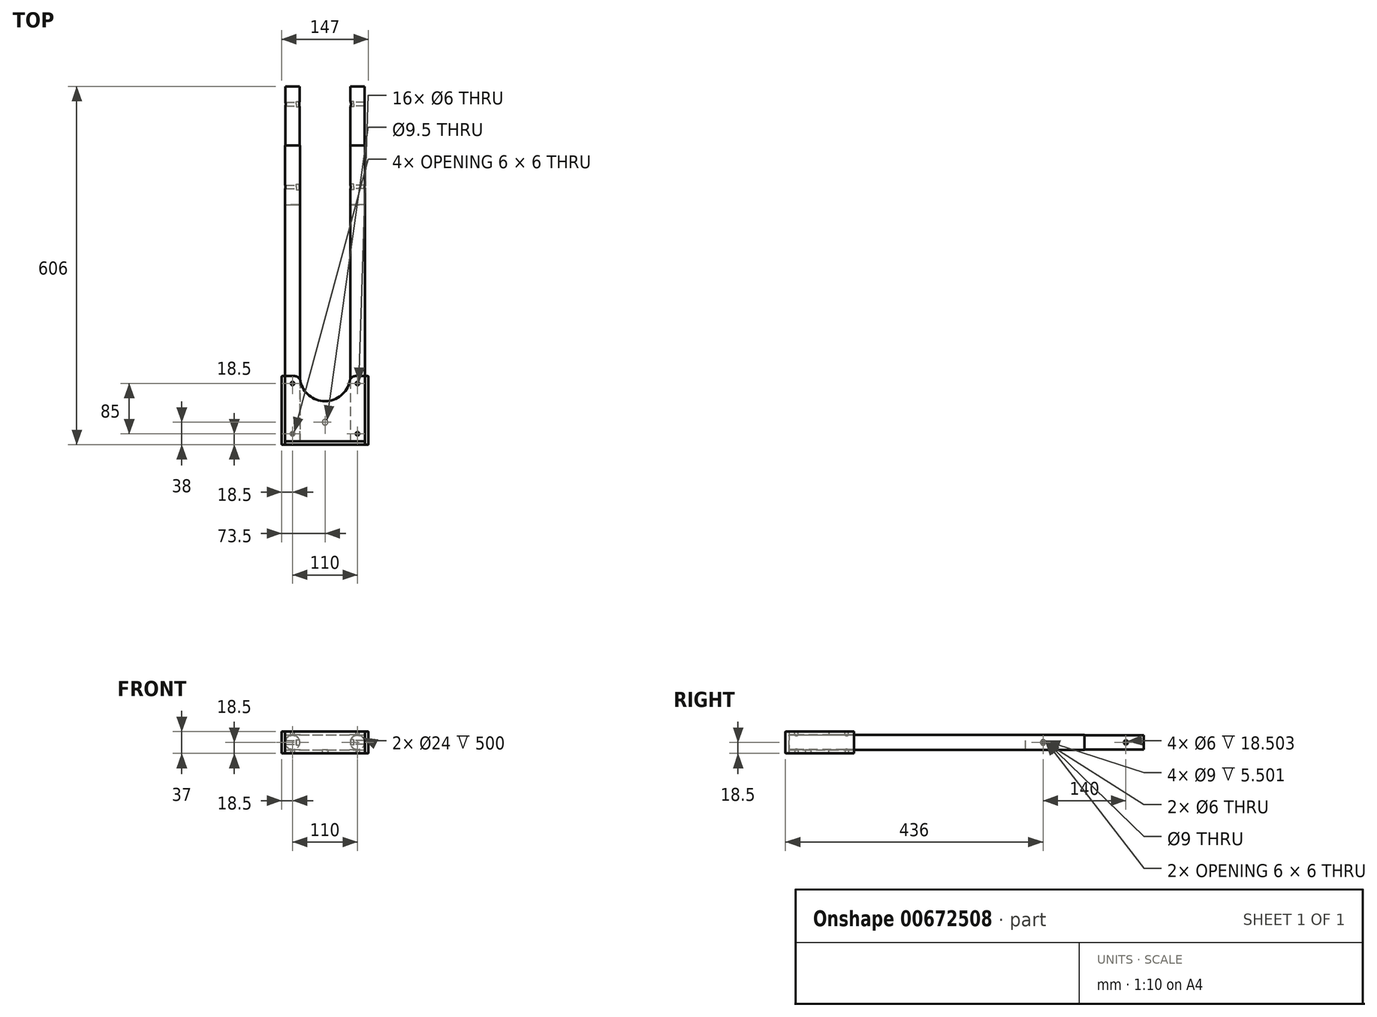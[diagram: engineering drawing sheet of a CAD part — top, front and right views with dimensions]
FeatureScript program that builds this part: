
annotation { "Feature Type Name" : "Feature", "Feature Type Description" : "" }
export const myFeature = defineFeature(function(context is Context, id is Id, definition is map)
    precondition{}
    {
        {
            var Q0;
            Q0=qCreatedBy(makeId("Front.planeOp"),FACE);
            var sketch = newSketch(context, id + "F0", { "sketchPlane" : qUnion([Q0])});
            skLineSegment(sketch, "E0", {"start": v(0, 0) * mm, "end": v(-55, 0) * mm, "construction": true});
            skCircle(sketch, "E1", {"center": v(-55, 0) * mm, "radius": 12.5 * mm});
            skCircle(sketch, "E2", {"center": v(-55, 0) * mm, "radius": 12 * mm});
            skSolve(sketch);
        }
        {
            var Q0;
            Q0=qSketchRegion(id+"F0",true);
            extrude(context, id + "F1", {"entities" : qUnion([Q0]), "oppositeDirection" : true, "depth" : 500 * mm, "offsetDistance" : 25 * mm});
        }
        {
            var Q0;
            Q0=qCreatedBy(makeId("Right.planeOp"),FACE);
            cPlane(context, id + "F2", {"entities" : qUnion([Q0]), "cplaneType" : CPlaneType.OFFSET, "offset" : 67.5 * mm, "oppositeDirection" : true, "width" : 150 * mm, "height" : 150 * mm});
        }
        {
            var Q0;
            Q0=qCreatedBy(id+"F2.planeOp",FACE);
            var sketch = newSketch(context, id + "F3", { "sketchPlane" : qUnion([Q0])});
            skCircle(sketch, "E3", {"center": v(430, 0) * mm, "radius": 3 * mm});
            skSolve(sketch);
        }
        {
            var Q0;
            Q0 = qSketchRegion(id + "F3", true);
            extrude(context, id + "F4", {"entities" : qUnion([Q0]), "operationType" : NewBodyOperationType.REMOVE, "depth" : 5 * mm, "offsetDistance" : 25 * mm});
        }
        {
            var Q0;
            Q0=makeQuery(id+"F1.opExtrude","SWEPT_BODY",BODY,{"disambiguationData":[OSD([sQuery(id+"F0.wireOp",EDGE,"E1"),sQuery(id+"F0.wireOp",EDGE,"E2")])]});
            var Q1;
            Q1=makeQuery(id+"FWwEWK0AGCShoOY_4.opExtrude","SWEPT_BODY",BODY,{"disambiguationData":[OSD([sQuery(id+"Fcy4laaUm5Z0fuw_4.wireOp",EDGE,"4f178126-5fd6-475b-9708-48581a11361a.0")])]});
            var Q2;
            Q2=qCreatedBy(makeId("Right.planeOp"),FACE);
            mirror(context, id + "F5", {"entities" : qUnion([Q0, Q1]), "mirrorPlane" : qUnion([Q2])});
        }
        {
            var Q0;
            Q0=qCreatedBy(makeId("Top.planeOp"),FACE);
            cPlane(context, id + "F6", {"entities" : qUnion([Q0]), "cplaneType" : CPlaneType.OFFSET, "offset" : 12.5 * mm, "oppositeDirection" : true, "width" : 150 * mm, "height" : 150 * mm});
        }
        {
            var Q0;
            Q0=qCreatedBy(id+"F6.planeOp",FACE);
            var sketch = newSketch(context, id + "F7", { "sketchPlane" : qUnion([Q0])});
            skLineSegment(sketch, "E4", {"start": v(-67.5, 0) * mm, "end": v(-67.5, 500) * mm, "construction": true});
            skLineSegment(sketch, "E5", {"start": v(67.5, 500) * mm, "end": v(67.5, 0) * mm, "construction": true});
            skLineSegment(sketch, "E6.top", {"start": v(-67.5, 110) * mm, "end": v(-42.5, 110) * mm});
            skLineSegment(sketch, "E6.left", {"start": v(-67.5, 0) * mm, "end": v(-67.5, 110) * mm});
            skLineSegment(sketch, "E6.right", {"start": v(67.5, 0) * mm, "end": v(67.5, 110) * mm});
            skArc(sketch, "E7", {"start": v(-42.5, 110) * mm, "mid": v(0, 67.5) * mm, "end": v(42.5, 110) * mm});
            skLineSegment(sketch, "E8.trimOffspring", {"start": v(42.5, 110) * mm, "end": v(67.5, 110) * mm});
            skLineSegment(sketch, "E9", {"start": v(-67.5, 0) * mm, "end": v(67.5, 0) * mm});
            skSolve(sketch);
        }
        {
            var Q0;
            Q0 = qSketchRegion(id + "F7", true);
            extrude(context, id + "F8", {"entities" : qUnion([Q0]), "oppositeDirection" : true, "depth" : 6 * mm, "offsetDistance" : 25 * mm});
        }
        {
            var Q0;
            Q0=makeQuery(id+"F8.opExtrude","SWEPT_EDGE",EDGE,{"disambiguationData":[OSD([sQuery(id+"F7.wireOp",EDGE,"E6.top"),sQuery(id+"F7.wireOp",EDGE,"E7")])]});
            var Q1;
            Q1=makeQuery(id+"F8.opExtrude","SWEPT_EDGE",EDGE,{"disambiguationData":[OSD([sQuery(id+"F7.wireOp",EDGE,"E7"),sQuery(id+"F7.wireOp",EDGE,"E8.trimOffspring")])]});
            fillet(context, id + "F9", {"entities" : qUnion([Q0, Q1]), "radius" : 10 * mm, "tangentPropagation" : true, "allowEdgeOverflow" : false});
        }
        {
            var Q0;
            Q0=makeQuery(id+"F8.opExtrude","CAP_FACE",FACE,{"disambiguationData":[OSD([sQuery(id+"F7.wireOp",EDGE,"E6.top"),sQuery(id+"F7.wireOp",EDGE,"E6.left"),sQuery(id+"F7.wireOp",EDGE,"E6.right"),sQuery(id+"F7.wireOp",EDGE,"E7"),sQuery(id+"F7.wireOp",EDGE,"E8.trimOffspring"),sQuery(id+"F7.wireOp",EDGE,"0f04a0eb-fee5-4bae-b65f-fa6f64b50764.0"),sQuery(id+"F7.wireOp",EDGE,"cbebf984-d675-44ab-9455-374cf201430f.0"),sQuery(id+"F7.wireOp",EDGE,"HSed2Bmm-BiSO-eANn-IlEf-6T3VpWwfTWnc")])],"isStart":false});
            var sketch = newSketch(context, id + "F10", { "sketchPlane" : qUnion([Q0])});
            skCircle(sketch, "E10", {"center": v(-55, -12.5) * mm, "radius": 3 * mm});
            skCircle(sketch, "E11", {"center": v(-55, -97.5) * mm, "radius": 3 * mm});
            skCircle(sketch, "E12", {"center": v(55, -97.5) * mm, "radius": 3 * mm});
            skCircle(sketch, "E13", {"center": v(55, -12.5) * mm, "radius": 3 * mm});
            skSolve(sketch);
        }
        {
            var Q0;
            Q0 = qSketchRegion(id + "F10", true);
            extrude(context, id + "F11", {"entities" : qUnion([Q0]), "operationType" : NewBodyOperationType.REMOVE, "endBound" : BoundingType.THROUGH_ALL, "oppositeDirection" : true, "depth" : 10 * mm, "offsetDistance" : 25 * mm});
        }
        {
            var Q0;
            Q0=makeQuery(id+"F8.opExtrude","SWEPT_BODY",BODY,{"disambiguationData":[OSD([sQuery(id+"F7.wireOp",EDGE,"E6.bottom"),sQuery(id+"F7.wireOp",EDGE,"E6.top"),sQuery(id+"F7.wireOp",EDGE,"E6.left"),sQuery(id+"F7.wireOp",EDGE,"E6.right"),sQuery(id+"F7.wireOp",EDGE,"E7"),sQuery(id+"F7.wireOp",EDGE,"E8.trimOffspring")])]});
            var Q1;
            Q1=qCreatedBy(makeId("Top.planeOp"),FACE);
            mirror(context, id + "F12", {"entities" : qUnion([Q0]), "mirrorPlane" : qUnion([Q1])});
        }
        {
            var Q0;
            Q0=makeQuery(id+"F5.opPattern","COPY",FACE,{"derivedFrom":makeQuery(id+"F1.opExtrude","CAP_FACE",FACE,{"disambiguationData":[OSD([sQuery(id+"F0.wireOp",EDGE,"E1"),sQuery(id+"F0.wireOp",EDGE,"E2")])],"isStart":false}),"instanceName":"1"});
            var sketch = newSketch(context, id + "F13", { "sketchPlane" : qUnion([Q0])});
            skCircle(sketch, "E14.0", {"center": v(-55, 0) * mm, "radius": 12 * mm});
            skSolve(sketch);
        }
        {
            var Q0;
            Q0 = qSketchRegion(id + "F13", true);
            extrude(context, id + "F14", {"entities" : qUnion([Q0]), "endBound" : BoundingType.SYMMETRIC, "depth" : 200 * mm, "offsetDistance" : 25 * mm});
        }
        {
            var Q0;
            Q0=qCreatedBy(makeId("Right.planeOp"),FACE);
            cPlane(context, id + "F15", {"entities" : qUnion([Q0]), "cplaneType" : CPlaneType.OFFSET, "offset" : 42.5 * mm, "width" : 150 * mm, "height" : 150 * mm});
        }
        {
            var Q0;
            Q0=qCreatedBy(id+"F15.planeOp",FACE);
            var sketch = newSketch(context, id + "F16", { "sketchPlane" : qUnion([Q0])});
            skLineSegment(sketch, "E15.0", {"start": v(400, 12) * mm, "end": v(400, -12) * mm, "construction": true});
            skCircle(sketch, "E16", {"center": v(430, 0) * mm, "radius": 3 * mm});
            skLineSegment(sketch, "E17.0", {"start": v(600, 12) * mm, "end": v(600, -12) * mm, "construction": true});
            skCircle(sketch, "E18", {"center": v(570, 0) * mm, "radius": 3 * mm});
            skSolve(sketch);
        }
        {
            var Q0;
            Q0 = qSketchRegion(id + "F16", true);
            extrude(context, id + "F17", {"entities" : qUnion([Q0]), "operationType" : NewBodyOperationType.REMOVE, "endBound" : BoundingType.THROUGH_ALL, "depth" : 25 * mm, "offsetDistance" : 25 * mm});
        }
        {
            var Q0;
            Q0=qCreatedBy(id+"F15.planeOp",FACE);
            var sketch = newSketch(context, id + "F18", { "sketchPlane" : qUnion([Q0])});
            skLineSegment(sketch, "E19", {"start": v(400, 12) * mm, "end": v(600, 12) * mm, "construction": true});
            skLineSegment(sketch, "E20", {"start": v(600, -12) * mm, "end": v(400, -12) * mm, "construction": true});
            skCircle(sketch, "E21.0", {"center": v(430, 0) * mm, "radius": 3 * mm, "construction": true});
            skCircle(sketch, "E22", {"center": v(430, 0) * mm, "radius": 4.5 * mm});
            skCircle(sketch, "E23.0", {"center": v(570, 0) * mm, "radius": 3 * mm, "construction": true});
            skCircle(sketch, "E24", {"center": v(570, 0) * mm, "radius": 4.5 * mm});
            skSolve(sketch);
        }
        {
            var Q0;
            Q0 = qSketchRegion(id + "F18", true);
            extrude(context, id + "F19", {"entities" : qUnion([Q0]), "operationType" : NewBodyOperationType.REMOVE, "depth" : 6 * mm, "offsetDistance" : 25 * mm});
        }
        {
            var Q0;
            Q0=makeQuery(id+"F14.opExtrude","SWEPT_BODY",BODY,{"disambiguationData":[OSD([sQuery(id+"F13.wireOp",EDGE,"E14.0")])]});
            var Q1;
            Q1=qCreatedBy(makeId("Right.planeOp"),FACE);
            mirror(context, id + "F20", {"entities" : qUnion([Q0]), "mirrorPlane" : qUnion([Q1])});
        }
        {
            var Q0;
            Q0=makeQuery(id+"F8.opExtrude","CAP_FACE",FACE,{"disambiguationData":[OSD([sQuery(id+"F7.wireOp",EDGE,"E6.top"),sQuery(id+"F7.wireOp",EDGE,"E6.left"),sQuery(id+"F7.wireOp",EDGE,"E6.right"),sQuery(id+"F7.wireOp",EDGE,"E7"),sQuery(id+"F7.wireOp",EDGE,"E8.trimOffspring"),sQuery(id+"F7.wireOp",EDGE,"d265e3d1-651c-44ed-b3ba-1d22781fd949.0"),sQuery(id+"F7.wireOp",EDGE,"8f73bf23-1377-4b1a-b3f5-81651f57eb4c.0"),sQuery(id+"F7.wireOp",EDGE,"ulxtdSOa-0rmS-N41F-JQdx-JKkltLVyDlMm"),sQuery(id+"F7.wireOp",EDGE,"lsUfgYp3-Q0MO-jZHI-4MhV-vEVjAvu659Rx"),sQuery(id+"F7.wireOp",EDGE,"MI6NjhT9-Nfcn-xXMY-YQLx-c0En6gxI8AMg")])],"isStart":false});
            var sketch = newSketch(context, id + "F21", { "sketchPlane" : qUnion([Q0])});
            skCircle(sketch, "E25", {"center": v(0, -32) * mm, "radius": 4.75 * mm});
            skSolve(sketch);
        }
        {
            var Q0;
            Q0 = qSketchRegion(id + "F21", true);
            extrude(context, id + "F22", {"entities" : qUnion([Q0]), "operationType" : NewBodyOperationType.REMOVE, "endBound" : BoundingType.UP_TO_NEXT, "oppositeDirection" : true, "depth" : 25 * mm, "offsetDistance" : 25 * mm});
        }
        {
            var Q0;
            Q0=makeQuery(id+"F12.opPattern","COPY",FACE,{"derivedFrom":makeQuery(id+"F8.opExtrude","SWEPT_FACE",FACE,{"disambiguationData":[OSD([sQuery(id+"F7.wireOp",EDGE,"E9")])]}),"instanceName":"1"});
            var sketch = newSketch(context, id + "F23", { "sketchPlane" : qUnion([Q0])});
            skPoint(sketch, "E26.0", {"position": v(67.5, -18.5) * mm});
            skLineSegment(sketch, "E27.bottom", {"start": v(-67.5, 18.5) * mm, "end": v(67.5, 18.5) * mm});
            skLineSegment(sketch, "E27.top", {"start": v(-67.5, -18.5) * mm, "end": v(67.5, -18.5) * mm});
            skLineSegment(sketch, "E27.left", {"start": v(-67.5, 18.5) * mm, "end": v(-67.5, -18.5) * mm});
            skLineSegment(sketch, "E27.right", {"start": v(67.5, 18.5) * mm, "end": v(67.5, -18.5) * mm});
            skSolve(sketch);
        }
        {
            var Q0;
            Q0 = qSketchRegion(id + "F23", true);
            extrude(context, id + "F24", {"entities" : qUnion([Q0]), "depth" : 6 * mm, "offsetDistance" : 25 * mm});
        }
        {
            var Q0;
            Q0=makeQuery(id+"F12.opPattern","COPY",FACE,{"derivedFrom":makeQuery(id+"F8.opExtrude","SWEPT_FACE",FACE,{"disambiguationData":[OSD([sQuery(id+"F7.wireOp",EDGE,"E6.left")])]}),"instanceName":"1"});
            var sketch = newSketch(context, id + "F25", { "sketchPlane" : qUnion([Q0])});
            skPoint(sketch, "E28.0", {"position": v(6, -18.5) * mm});
            skLineSegment(sketch, "E29.bottom", {"start": v(-110, 18.5) * mm, "end": v(6, 18.5) * mm});
            skLineSegment(sketch, "E29.top", {"start": v(-110, -18.5) * mm, "end": v(6, -18.5) * mm});
            skLineSegment(sketch, "E29.left", {"start": v(-110, 18.5) * mm, "end": v(-110, -18.5) * mm});
            skLineSegment(sketch, "E29.right", {"start": v(6, 18.5) * mm, "end": v(6, -18.5) * mm});
            skSolve(sketch);
        }
        {
            var Q0;
            Q0 = qSketchRegion(id + "F25", true);
            extrude(context, id + "F26", {"entities" : qUnion([Q0]), "depth" : 6 * mm, "offsetDistance" : 25 * mm});
        }
        {
            var Q0;
            Q0=makeQuery(id+"F26.opExtrude","SWEPT_BODY",BODY,{"disambiguationData":[OSD([sQuery(id+"F25.wireOp",EDGE,"E29.bottom"),sQuery(id+"F25.wireOp",EDGE,"E29.top"),sQuery(id+"F25.wireOp",EDGE,"E29.left"),sQuery(id+"F25.wireOp",EDGE,"E29.right")])]});
            var Q1;
            Q1=qCreatedBy(makeId("Right.planeOp"),FACE);
            mirror(context, id + "F27", {"entities" : qUnion([Q0]), "mirrorPlane" : qUnion([Q1])});
        }
        {
            var Q0;
            Q0=makeQuery(id+"F24.opExtrude","CAP_EDGE",EDGE,{"disambiguationData":[OSD([sQuery(id+"F23.wireOp",EDGE,"E27.bottom")])],"isStart":false});
            var Q1;
            Q1=makeQuery(id+"F27.opPattern","COPY",EDGE,{"derivedFrom":makeQuery(id+"F26.opExtrude","CAP_EDGE",EDGE,{"disambiguationData":[OSD([sQuery(id+"F25.wireOp",EDGE,"E29.bottom")])],"isStart":false}),"instanceName":"1"});
            var Q2;
            Q2=makeQuery(id+"F27.opPattern","COPY",EDGE,{"derivedFrom":makeQuery(id+"F26.opExtrude","SWEPT_EDGE",EDGE,{"disambiguationData":[OSD([sQuery(id+"F25.wireOp",EDGE,"E29.bottom"),sQuery(id+"F25.wireOp",EDGE,"E29.right")])]}),"instanceName":"1"});
            var Q3;
            Q3=makeQuery(id+"F27.opPattern","COPY",EDGE,{"derivedFrom":makeQuery(id+"F26.opExtrude","CAP_EDGE",EDGE,{"disambiguationData":[OSD([sQuery(id+"F25.wireOp",EDGE,"E29.right")])],"isStart":false}),"instanceName":"1"});
            var Q4;
            Q4=makeQuery(id+"F27.opPattern","COPY",EDGE,{"derivedFrom":makeQuery(id+"F26.opExtrude","CAP_EDGE",EDGE,{"disambiguationData":[OSD([sQuery(id+"F25.wireOp",EDGE,"E29.left")])],"isStart":false}),"instanceName":"1"});
            var Q5;
            Q5=makeQuery(id+"F27.opPattern","COPY",EDGE,{"derivedFrom":makeQuery(id+"F26.opExtrude","CAP_EDGE",EDGE,{"disambiguationData":[OSD([sQuery(id+"F25.wireOp",EDGE,"E29.top")])],"isStart":false}),"instanceName":"1"});
            var Q6;
            Q6=makeQuery(id+"F24.opExtrude","CAP_EDGE",EDGE,{"disambiguationData":[OSD([sQuery(id+"F23.wireOp",EDGE,"E27.top")])],"isStart":false});
            var Q7;
            Q7=makeQuery(id+"F27.opPattern","COPY",EDGE,{"derivedFrom":makeQuery(id+"F26.opExtrude","SWEPT_EDGE",EDGE,{"disambiguationData":[OSD([sQuery(id+"F25.wireOp",EDGE,"E29.top"),sQuery(id+"F25.wireOp",EDGE,"E29.right")])]}),"instanceName":"1"});
            var Q8;
            Q8=makeQuery(id+"F26.opExtrude","SWEPT_EDGE",EDGE,{"disambiguationData":[OSD([sQuery(id+"F25.wireOp",EDGE,"E29.top"),sQuery(id+"F25.wireOp",EDGE,"E29.right")])]});
            var Q9;
            Q9=makeQuery(id+"F26.opExtrude","CAP_EDGE",EDGE,{"disambiguationData":[OSD([sQuery(id+"F25.wireOp",EDGE,"E29.right")])],"isStart":false});
            var Q10;
            Q10=makeQuery(id+"F26.opExtrude","SWEPT_EDGE",EDGE,{"disambiguationData":[OSD([sQuery(id+"F25.wireOp",EDGE,"E29.bottom"),sQuery(id+"F25.wireOp",EDGE,"E29.right")])]});
            var Q11;
            Q11=makeQuery(id+"F26.opExtrude","CAP_EDGE",EDGE,{"disambiguationData":[OSD([sQuery(id+"F25.wireOp",EDGE,"E29.bottom")])],"isStart":false});
            var Q12;
            Q12=makeQuery(id+"F26.opExtrude","CAP_EDGE",EDGE,{"disambiguationData":[OSD([sQuery(id+"F25.wireOp",EDGE,"E29.top")])],"isStart":false});
            var Q13;
            Q13=makeQuery(id+"F26.opExtrude","CAP_EDGE",EDGE,{"disambiguationData":[OSD([sQuery(id+"F25.wireOp",EDGE,"E29.left")])],"isStart":false});
            var Q14;
            Q14=makeQuery(id+"F26.opExtrude","SWEPT_EDGE",EDGE,{"disambiguationData":[OSD([sQuery(id+"F25.wireOp",EDGE,"E29.bottom"),sQuery(id+"F25.wireOp",EDGE,"E29.left")])]});
            var Q15;
            Q15=makeQuery(id+"F12.opPattern","COPY",EDGE,{"derivedFrom":makeQuery(id+"F8.opExtrude","CAP_EDGE",EDGE,{"disambiguationData":[OSD([sQuery(id+"F7.wireOp",EDGE,"E6.top")])],"isStart":false}),"instanceName":"1"});
            var Q16;
            {var subQ0=sQuery(id+"F7.wireOp",EDGE,"E7");var subQ1=sQuery(id+"F7.wireOp",EDGE,"E6.top");Q16=makeQuery(id+"F12.opPattern","COPY",EDGE,{"derivedFrom":makeQuery(id+"F9.opFillet","BLEND_EDGE",EDGE,{"blendedFrom":[makeQuery(id+"F8.opExtrude","SWEPT_EDGE",EDGE,{"disambiguationData":[OSD([subQ1,subQ0])]}),makeQuery(id+"F8.opExtrude","CAP_FACE",FACE,{"disambiguationData":[OSD([subQ1,sQuery(id+"F7.wireOp",EDGE,"E6.left"),sQuery(id+"F7.wireOp",EDGE,"E6.right"),subQ0,sQuery(id+"F7.wireOp",EDGE,"E8.trimOffspring"),sQuery(id+"F7.wireOp",EDGE,"E9")])],"isStart":false})],"blendedInto":[makeQuery(id+"F8.opExtrude","CAP_FACE",FACE,{"disambiguationData":[OSD([subQ1,sQuery(id+"F7.wireOp",EDGE,"E6.left"),sQuery(id+"F7.wireOp",EDGE,"E6.right"),subQ0,sQuery(id+"F7.wireOp",EDGE,"E8.trimOffspring"),sQuery(id+"F7.wireOp",EDGE,"E9")])],"isStart":false})]}),"instanceName":"1"});}
            var Q17;
            Q17=makeQuery(id+"F27.opPattern","COPY",EDGE,{"derivedFrom":makeQuery(id+"F26.opExtrude","SWEPT_EDGE",EDGE,{"disambiguationData":[OSD([sQuery(id+"F25.wireOp",EDGE,"E29.bottom"),sQuery(id+"F25.wireOp",EDGE,"E29.left")])]}),"instanceName":"1"});
            var Q18;
            Q18=makeQuery(id+"F27.opPattern","COPY",EDGE,{"derivedFrom":makeQuery(id+"F26.opExtrude","SWEPT_EDGE",EDGE,{"disambiguationData":[OSD([sQuery(id+"F25.wireOp",EDGE,"E29.top"),sQuery(id+"F25.wireOp",EDGE,"E29.left")])]}),"instanceName":"1"});
            var Q19;
            Q19=makeQuery(id+"F8.opExtrude","CAP_EDGE",EDGE,{"disambiguationData":[OSD([sQuery(id+"F7.wireOp",EDGE,"E8.trimOffspring")])],"isStart":false});
            fillet(context, id + "F28", {"entities" : qUnion([Q0, Q1, Q2, Q3, Q4, Q5, Q6, Q7, Q8, Q9, Q10, Q11, Q12, Q13, Q14, Q15, Q16, Q17, Q18, Q19]), "radius" : 1 * mm, "tangentPropagation" : true, "allowEdgeOverflow" : false});
        }
    });
